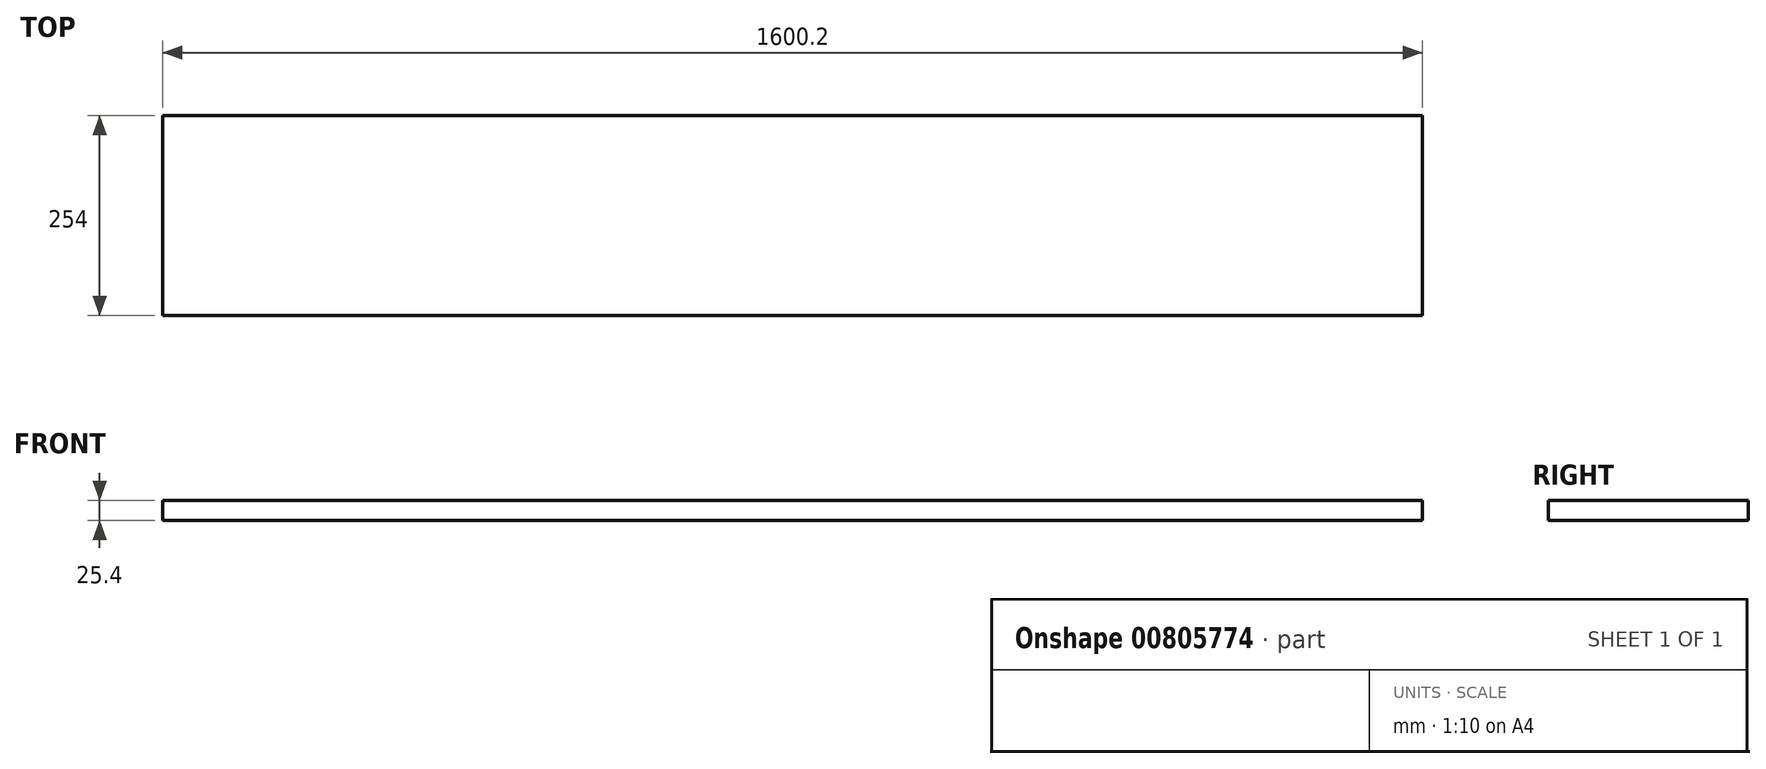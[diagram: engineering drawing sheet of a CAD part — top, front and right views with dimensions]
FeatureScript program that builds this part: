
annotation { "Feature Type Name" : "Feature", "Feature Type Description" : "" }
export const myFeature = defineFeature(function(context is Context, id is Id, definition is map)
    precondition{}
    {
        {
            var Q0;
            Q0=qCreatedBy(makeId("Top.planeOp"),FACE);
            var sketch = newSketch(context, id + "F0", { "sketchPlane" : qUnion([Q0])});
            skLineSegment(sketch, "E0.bottom", {"start": v(0, 0) * mm, "end": v(1600.2, 0) * mm});
            skLineSegment(sketch, "E0.top", {"start": v(0, 254) * mm, "end": v(1600.2, 254) * mm});
            skLineSegment(sketch, "E0.left", {"start": v(0, 0) * mm, "end": v(0, 254) * mm});
            skLineSegment(sketch, "E0.right", {"start": v(1600.2, 0) * mm, "end": v(1600.2, 254) * mm});
            skSolve(sketch);
        }
        {
            var Q0;
            Q0 = qSketchRegion(id + "F0", true);
            extrude(context, id + "F1", {"entities" : qUnion([Q0]), "depth" : 25.4 * mm, "offsetDistance" : 25.4 * mm});
        }
    });
